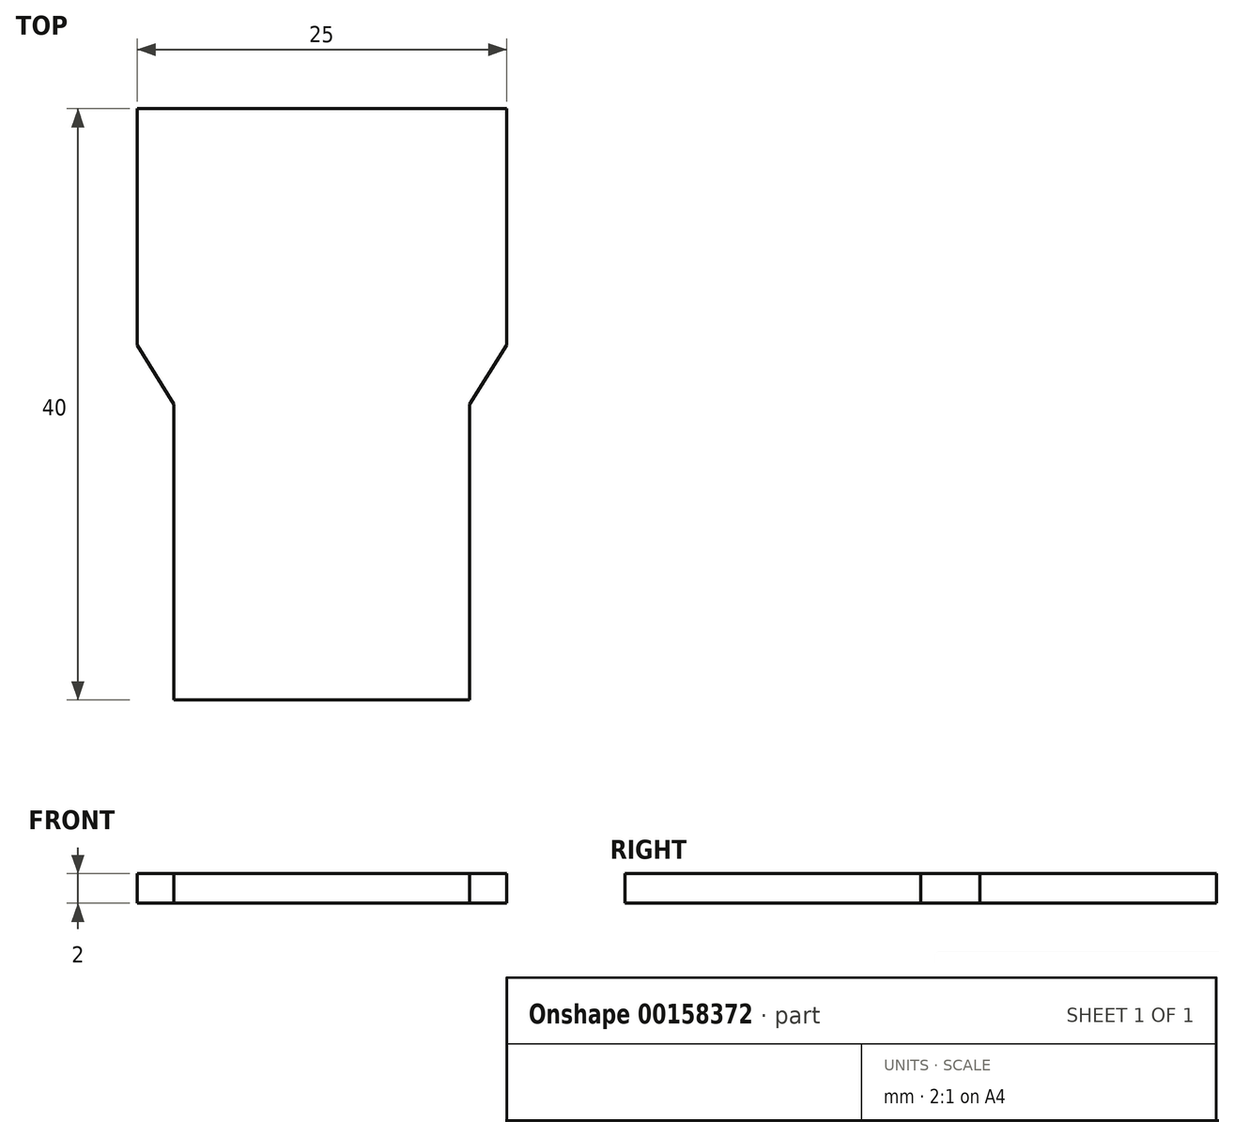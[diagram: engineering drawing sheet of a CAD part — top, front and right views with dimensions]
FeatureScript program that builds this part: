
annotation { "Feature Type Name" : "Feature", "Feature Type Description" : "" }
export const myFeature = defineFeature(function(context is Context, id is Id, definition is map)
    precondition{}
    {
        {
            var Q0;
            Q0=qCreatedBy(makeId("Top.planeOp"),FACE);
            var sketch = newSketch(context, id + "F0", { "sketchPlane" : qUnion([Q0])});
            skLineSegment(sketch, "E0", {"start": v(0, 0) * mm, "end": v(10, 0) * mm});
            skLineSegment(sketch, "E1", {"start": v(10, 0) * mm, "end": v(10, 20) * mm});
            skLineSegment(sketch, "E2", {"start": v(10, 20) * mm, "end": v(12.5, 24) * mm});
            skLineSegment(sketch, "E3", {"start": v(12.5, 24) * mm, "end": v(12.5, 40) * mm});
            skLineSegment(sketch, "E4", {"start": v(12.5, 40) * mm, "end": v(0, 40) * mm});
            skLineSegment(sketch, "E5.MirrorCS", {"start": v(-12.5, 40) * mm, "end": v(0, 40) * mm});
            skLineSegment(sketch, "E6.MirrorCS", {"start": v(-12.5, 24) * mm, "end": v(-12.5, 40) * mm});
            skLineSegment(sketch, "E7.MirrorCS", {"start": v(-10, 0) * mm, "end": v(-10, 20) * mm});
            skLineSegment(sketch, "E8.MirrorCS", {"start": v(-10, 20) * mm, "end": v(-12.5, 24) * mm});
            skLineSegment(sketch, "E9.MirrorCS", {"start": v(0, 0) * mm, "end": v(-10, 0) * mm});
            skSolve(sketch);
        }
        {
            var Q0;
            Q0=makeQuery(id+"F0.imprint","IMPRINT",FACE,{"disambiguationData":[TD([[makeQuery(id+"F0.imprint","IMPRINT",EDGE,{"derivedFrom":sQuery(id+"F0.wireOp",EDGE,"E0")}),1.0]])]});
            extrude(context, id + "F1", {"entities" : qUnion([Q0]), "depth" : 2 * mm, "offsetDistance" : 25 * mm});
        }
    });
